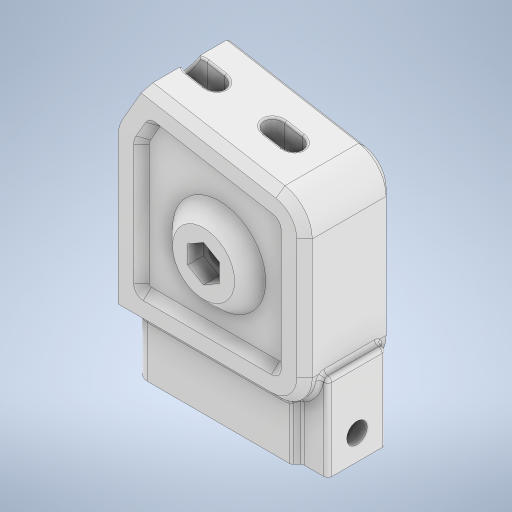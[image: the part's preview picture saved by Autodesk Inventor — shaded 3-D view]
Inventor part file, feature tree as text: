
AUTODESK INVENTOR PART (.ipt)
format: ipt  version: 2024 (Build 280153000, 153)  size: 863,232 bytes
history: native  units: mm
features: fillet x14, sketch x13, extrude x12, projected_geometry x9, chamfer x5, plane x3, hole x2, mirror x2
ambient origin geometry x8: Origin, YZ Plane, XZ Plane, XY Plane, X Axis, Y Axis, Z Axis, Center Point
bodies: Solid1 (feature_tree)
feature tree (60):
  extrude  "Extrusion1"  Depth=48.0mm
  sketch  "Sketch4"  dims[d2=31.0mm d3=31.0mm d4=19.198622mm d5=150.0deg d6=23.0mm d7=0.0mm]
  plane  "Work Plane1"
  plane  "Work Plane2"
  extrude  "Extrusion4"  Depth=31.0mm
  fillet  "Fillet1"  Radius=19.198622mm
  fillet  "Fillet2"  [1 undecoded]
  fillet  "Fillet8"  Radius=23.0mm
  chamfer  "Chamfer3"  Distance=16.0mm
  extrude  "Extrusion8"  Depth=1.0mm
  chamfer  "Chamfer9"  Distance=2.0mm Angle=45.0deg
  hole  "Hole7"  [1 undecoded]
  extrude  "Extrusion11"  Depth=9.0mm
  mirror  "Mirror2"
  fillet  "Fillet17"  Radius=9.0mm
  extrude  "Extrusion12"  Depth=4.0mm
  extrude  "Extrusion14"  Depth=16.0mm
  chamfer  "Chamfer6"  Distance=2.0mm
  chamfer  "Chamfer7"  Distance=2.0mm Angle=45.0deg
  chamfer  "Chamfer8"  Distance=2.0mm
  extrude  "Extrusion13"  Depth=4.0mm TaperAngle=45.0deg
  extrude  "Extrusion15"  Depth=0.5mm
  fillet  "Fillet19"  Radius=4.0mm
  mirror  "Mirror3"
  sketch  "Sketch10"  dims[d23=-3.75mm]
  extrude  "Extrusion16"  Depth=1.0mm TaperAngle=0.0deg
  extrude  "Extrusion17"  Depth=1.0mm TaperAngle=45.0deg
  extrude  "Extrusion18"  Depth=0.5mm
  fillet  "Fillet26"  Radius=0.5mm
  fillet  "Fillet27"  Radius=0.5mm
  fillet  "Fillet28"  Radius=2.65mm
  fillet  "Fillet29"  Radius=4.5mm
  fillet  "Fillet30"  Radius=10.0mm
  hole  "Hole9"  [1 undecoded]
  fillet  "Fillet31"  [1 undecoded]
  plane  "Work Plane7"
  extrude  "Extrusion21"  Depth=0.5mm
  fillet  "Fillet32"  Radius=15.0mm
  fillet  "Fillet35"  Radius=1.5mm
  fillet  "Fillet36"  Radius=20.0mm
  sketch  "Sketch1"  dims[d0=48.0mm d1=48.0mm]
  sketch  "Sketch9"  dims[d20=23.0mm]
  projected_geometry  "Projected Loop2"
  sketch  "Sketch12"  dims[d24=-3.75mm d25=16.0mm d26=0.0mm]
  sketch  "Sketch14"  dims[d27=1.0mm d28=1.0mm]
  projected_geometry  "Projected Loop6"
  sketch  "Sketch15"  dims[d67=8.5mm d68=2.0mm d69=2.0mm d70=45.0deg]
  projected_geometry  "Projected Loop7"
  sketch  "Sketch16"  dims[d73=18.0mm d74=40.0mm]
  sketch  "Sketch18"  dims[d75=14.0mm d76=0.0mm d80=9.0mm d81=9.0mm]
  projected_geometry  "Projected Loop8"
  sketch  "Sketch19"  dims[d82=9.0mm]
  sketch  "Sketch20"  dims[d110=5.4mm d111=6.0mm d112=4.0mm d113=2.0mm d114=90.0deg d115=8.0mm d116=20.594885mm d130=4.0mm]
  projected_geometry  "Projected Loop9"
  projected_geometry  "Projected Loop10"
  sketch  "Sketch22"  dims[d131=8.0mm d132=0.0mm d133=16.0mm d134=2.0mm d135=0.0mm]
  projected_geometry  "Projected Loop12"
  sketch  "Sketch23"  dims[d136=2.5mm d137=2.0mm d138=2.0mm d139=45.0deg d140=2.0mm d141=0.0mm d142=4.0mm d143=2.0mm d144=45.0deg d145=8.2mm d146=4.0mm d147=0.0mm d156=1.0mm d157=0.0mm d158=1.0mm d159=2.0mm d160=45.0deg d161=8.0mm d162=0.5mm d163=0.0mm d164=0.5mm d165=2.65mm d166=4.5mm d167=10.0mm d168=0.0mm d170=40.0mm d171=0.0mm d172=0.0mm d173=0.0mm d186=8.0mm d187=15.0mm d188=1.5mm d189=2.0mm d190=45.0deg d191=20.0mm d192=10.0mm d193=1.0mm d194=1.0mm d195=3.0mm d196=1.0mm d197=0.5mm d198=2.0mm d199=5.75mm d200=5.3mm d201=6.0mm d202=4.0mm d203=2.0mm d204=90.0deg d205=1.0mm d206=0.0mm d207=0.5mm d208=-9.0mm d213=0.5mm d216=1.0mm d217=8.25mm d218=4.0mm d219=0.0mm d220=1.0mm d221=3.5mm d222=10.0mm d174=0.5mm d175=0.872665mm]
  projected_geometry  "Project Cut Edges1"
  projected_geometry  "Project Cut Edges2"
note: 4 required parameter values undecoded (feature->parameter linkage not recoverable at this tier; creation-order binding heuristic only, values carry confidence <= 0.55)
